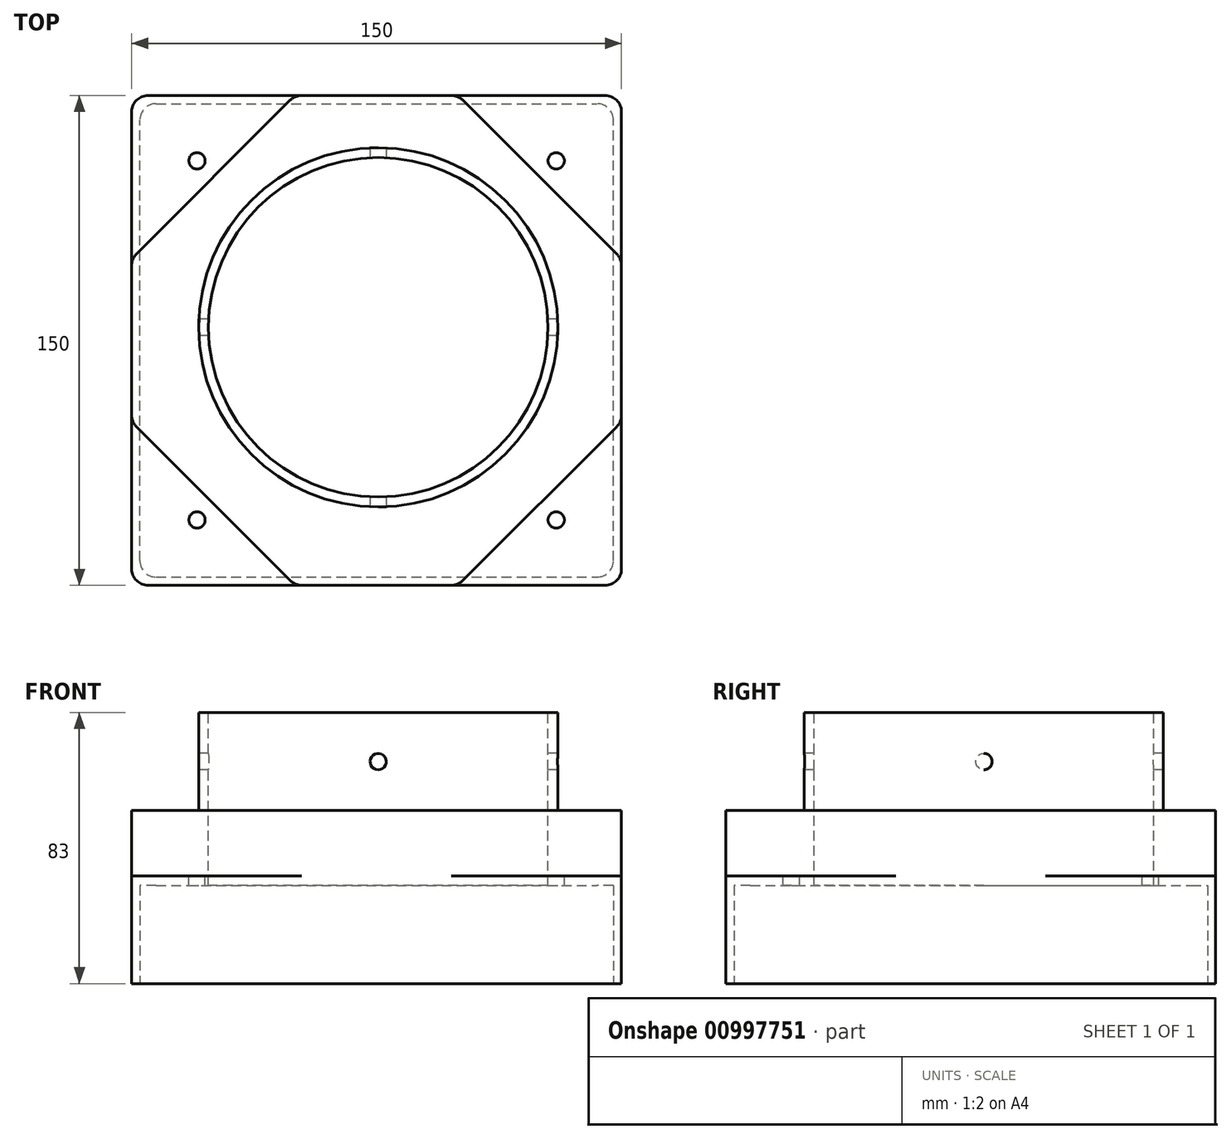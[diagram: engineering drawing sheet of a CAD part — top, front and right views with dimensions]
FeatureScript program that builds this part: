
annotation { "Feature Type Name" : "Feature", "Feature Type Description" : "" }
export const myFeature = defineFeature(function(context is Context, id is Id, definition is map)
    precondition{}
    {
        {
            var Q0;
            Q0=qCreatedBy(makeId("Top.planeOp"),FACE);
            var sketch = newSketch(context, id + "F0", { "sketchPlane" : qUnion([Q0])});
            skLineSegment(sketch, "E0.bottom", {"start": v(-75.5, 71) * mm, "end": v(74.5, 71) * mm});
            skLineSegment(sketch, "E0.top", {"start": v(-75.5, -79) * mm, "end": v(74.5, -79) * mm});
            skLineSegment(sketch, "E0.left", {"start": v(-75.5, 71) * mm, "end": v(-75.5, -79) * mm});
            skLineSegment(sketch, "E0.right", {"start": v(74.5, 71) * mm, "end": v(74.5, -79) * mm});
            skSolve(sketch);
        }
        {
            var Q0;
            Q0=makeQuery(id+"F0.imprint","IMPRINT",FACE,{"disambiguationData":[TD([[makeQuery(id+"F0.imprint","IMPRINT",EDGE,{"derivedFrom":sQuery(id+"F0.wireOp",EDGE,"E0.bottom")}),-1.0]])]});
            extrude(context, id + "F1", {"entities" : qUnion([Q0]), "depth" : 33 * mm, "offsetDistance" : 25 * mm});
        }
        {
            var Q0;
            Q0=makeQuery(id+"F1.opExtrude","CAP_FACE",FACE,{"disambiguationData":[OSD([sQuery(id+"F0.wireOp",EDGE,"E0.bottom"),sQuery(id+"F0.wireOp",EDGE,"E0.top"),sQuery(id+"F0.wireOp",EDGE,"E0.left"),sQuery(id+"F0.wireOp",EDGE,"E0.right")])],"isStart":false});
            var sketch = newSketch(context, id + "F2", { "sketchPlane" : qUnion([Q0])});
            skLineSegment(sketch, "E1.0", {"start": v(-8.5, 88) * mm, "end": v(7.5, 88) * mm});
            skLineSegment(sketch, "E1.1", {"start": v(7.5, 88) * mm, "end": v(91.5, 4) * mm});
            skLineSegment(sketch, "E1.2", {"start": v(91.5, 4) * mm, "end": v(91.5, -12) * mm});
            skLineSegment(sketch, "E1.3", {"start": v(91.5, -12) * mm, "end": v(7.5, -96) * mm});
            skLineSegment(sketch, "E1.4", {"start": v(7.5, -96) * mm, "end": v(-8.5, -96) * mm});
            skLineSegment(sketch, "E1.5", {"start": v(-8.5, -96) * mm, "end": v(-92.5, -12) * mm});
            skLineSegment(sketch, "E1.6", {"start": v(-92.5, -12) * mm, "end": v(-92.5, 4) * mm});
            skLineSegment(sketch, "E1.7", {"start": v(-92.5, 4) * mm, "end": v(-8.5, 88) * mm});
            skPoint(sketch, "E1.0.midPoint", {"position": v(-0.5, 88) * mm});
            skPoint(sketch, "E2", {"position": v(-25.5, 71) * mm});
            skPoint(sketch, "E3", {"position": v(24.5, -79) * mm});
            skPoint(sketch, "E4", {"position": v(-75.5, -29) * mm});
            skPoint(sketch, "E5", {"position": v(24.5, 71) * mm});
            skPoint(sketch, "E6", {"position": v(-75.5, 21) * mm});
            skPoint(sketch, "E7", {"position": v(74.5, 21) * mm});
            skPoint(sketch, "E8", {"position": v(74.5, -29) * mm});
            skPoint(sketch, "E9", {"position": v(-25.5, -79) * mm});
            skSolve(sketch);
        }
        {
            var Q0;
            {var subQ3=makeQuery(id+"F1.opExtrude","CAP_EDGE",EDGE,{"disambiguationData":[OSD([sQuery(id+"F0.wireOp",EDGE,"E0.bottom")])],"isStart":false});var subQ13=sQuery(id+"F2.wireOp",EDGE,"E1.1");var subQ14=makeQuery(id+"F2.imprint","INTERSECT",VERTEX,{"derivedFrom":[subQ3,subQ13]});Q0=makeQuery(id+"F2.imprint","IMPRINT",FACE,{"disambiguationData":[TD([[makeQuery(id+"F2.imprint","IMPRINT",EDGE,{"disambiguationData":[TD([[subQ14,-1.0]])],"derivedFrom":subQ13}),-1.0]])]});}
            extrude(context, id + "F3", {"entities" : qUnion([Q0]), "operationType" : NewBodyOperationType.ADD, "depth" : 20 * mm, "offsetDistance" : 25 * mm});
        }
        {
            var Q0;
            Q0=makeQuery(id+"F1.opExtrude","SWEPT_EDGE",EDGE,{"disambiguationData":[OSD([sQuery(id+"F0.wireOp",EDGE,"E0.bottom"),sQuery(id+"F0.wireOp",EDGE,"E0.left")])]});
            var Q1;
            Q1=makeQuery(id+"F1.opExtrude","SWEPT_EDGE",EDGE,{"disambiguationData":[OSD([sQuery(id+"F0.wireOp",EDGE,"E0.top"),sQuery(id+"F0.wireOp",EDGE,"E0.left")])]});
            var Q2;
            Q2=makeQuery(id+"F1.opExtrude","SWEPT_EDGE",EDGE,{"disambiguationData":[OSD([sQuery(id+"F0.wireOp",EDGE,"E0.bottom"),sQuery(id+"F0.wireOp",EDGE,"E0.right")])]});
            var Q3;
            Q3=makeQuery(id+"F1.opExtrude","SWEPT_EDGE",EDGE,{"disambiguationData":[OSD([sQuery(id+"F0.wireOp",EDGE,"E0.top"),sQuery(id+"F0.wireOp",EDGE,"E0.right")])]});
            fillet(context, id + "F4", {"entities" : qUnion([Q0, Q1, Q2, Q3]), "radius" : 5 * mm, "tangentPropagation" : true, "allowEdgeOverflow" : false});
        }
        {
            var Q0;
            Q0=makeQuery(id+"F3.opExtrude","CAP_FACE",FACE,{"disambiguationData":[OSD([sQuery(id+"F0.wireOp",EDGE,"E0.bottom"),sQuery(id+"F0.wireOp",EDGE,"E0.top"),sQuery(id+"F0.wireOp",EDGE,"E0.left"),sQuery(id+"F0.wireOp",EDGE,"E0.right"),sQuery(id+"F2.wireOp",EDGE,"E1.1"),sQuery(id+"F2.wireOp",EDGE,"E1.3"),sQuery(id+"F2.wireOp",EDGE,"E1.5"),sQuery(id+"F2.wireOp",EDGE,"E1.7")])],"isStart":false});
            var sketch = newSketch(context, id + "F5", { "sketchPlane" : qUnion([Q0])});
            skCircle(sketch, "E10", {"center": v(0, 0) * mm, "radius": 55 * mm});
            skSolve(sketch);
        }
        {
            var Q0;
            Q0 = qSketchRegion(id + "F5", true);
            extrude(context, id + "F6", {"entities" : qUnion([Q0]), "operationType" : NewBodyOperationType.ADD, "depth" : 30 * mm, "offsetDistance" : 25 * mm});
        }
        {
            var Q0;
            Q0=makeQuery(id+"F1.opExtrude","CAP_FACE",FACE,{"disambiguationData":[OSD([sQuery(id+"F0.wireOp",EDGE,"E0.bottom"),sQuery(id+"F0.wireOp",EDGE,"E0.top"),sQuery(id+"F0.wireOp",EDGE,"E0.left"),sQuery(id+"F0.wireOp",EDGE,"E0.right")])],"isStart":true});
            var sketch = newSketch(context, id + "F7", { "sketchPlane" : qUnion([Q0])});
            skLineSegment(sketch, "E11.bottom", {"start": v(-68, 76.5) * mm, "end": v(67, 76.5) * mm});
            skLineSegment(sketch, "E11.top", {"start": v(-68, -68.5) * mm, "end": v(67, -68.5) * mm});
            skLineSegment(sketch, "E11.left", {"start": v(-73, 71.5) * mm, "end": v(-73, -63.5) * mm});
            skLineSegment(sketch, "E11.right", {"start": v(72, 71.5) * mm, "end": v(72, -63.5) * mm});
            skPoint(sketch, "E12.visualSharp", {"position": v(-73, 76.5) * mm});
            skArc(sketch, "E12.filletArc", {"start": v(-68, 76.5) * mm, "mid": v(-71.54, 75.04) * mm, "end": v(-73, 71.5) * mm});
            skPoint(sketch, "E13.visualSharp", {"position": v(72, 76.5) * mm});
            skArc(sketch, "E13.filletArc", {"start": v(72, 71.5) * mm, "mid": v(70.54, 75.04) * mm, "end": v(67, 76.5) * mm});
            skPoint(sketch, "E14.visualSharp", {"position": v(72, -68.5) * mm});
            skArc(sketch, "E14.filletArc", {"start": v(67, -68.5) * mm, "mid": v(70.54, -67.03) * mm, "end": v(72, -63.5) * mm});
            skPoint(sketch, "E15.visualSharp", {"position": v(-73, -68.5) * mm});
            skArc(sketch, "E15.filletArc", {"start": v(-73, -63.5) * mm, "mid": v(-71.54, -67.03) * mm, "end": v(-68, -68.5) * mm});
            skSolve(sketch);
        }
        {
            var Q0;
            Q0=makeQuery(id+"F7.imprint","IMPRINT",FACE,{"disambiguationData":[TD([[makeQuery(id+"F7.imprint","IMPRINT",EDGE,{"derivedFrom":sQuery(id+"F7.wireOp",EDGE,"E11.bottom")}),-1.0]])]});
            extrude(context, id + "F8", {"entities" : qUnion([Q0]), "operationType" : NewBodyOperationType.REMOVE, "oppositeDirection" : true, "depth" : 30 * mm, "offsetDistance" : 25 * mm});
        }
        {
            var Q0;
            Q0=makeQuery(id+"F6.opExtrude","CAP_FACE",FACE,{"disambiguationData":[OSD([sQuery(id+"F5.wireOp",EDGE,"E10")])],"isStart":false});
            var sketch = newSketch(context, id + "F9", { "sketchPlane" : qUnion([Q0])});
            skCircle(sketch, "E16", {"center": v(0, 0) * mm, "radius": 52 * mm});
            skSolve(sketch);
        }
        {
            var Q0;
            Q0=makeQuery(id+"F9.imprint","IMPRINT",FACE,{"disambiguationData":[TD([[makeQuery(id+"F9.imprint","IMPRINT",EDGE,{"derivedFrom":sQuery(id+"F9.wireOp",EDGE,"E16")}),1.0]])]});
            extrude(context, id + "F10", {"entities" : qUnion([Q0]), "operationType" : NewBodyOperationType.REMOVE, "endBound" : BoundingType.THROUGH_ALL, "oppositeDirection" : true, "depth" : 25 * mm, "offsetDistance" : 25 * mm});
        }
        {
            var Q0;
            {var subQ0=sQuery(id+"F0.wireOp",EDGE,"E0.bottom");var subQ1=sQuery(id+"F0.wireOp",EDGE,"E0.left");Q0=makeQuery(id+"F3.boolean.opBoolean","SPLIT",FACE,{"disambiguationData":[TD([makeQuery(id+"F3.opExtrude","SWEPT_FACE",FACE,{"disambiguationData":[OSD([sQuery(id+"F2.wireOp",EDGE,"E1.7")])]})])],"derivedFrom":makeQuery(id+"F1.opExtrude","CAP_FACE",FACE,{"disambiguationData":[OSD([subQ0,sQuery(id+"F0.wireOp",EDGE,"E0.top"),subQ1,sQuery(id+"F0.wireOp",EDGE,"E0.right")])],"isStart":false})});}
            var sketch = newSketch(context, id + "F11", { "sketchPlane" : qUnion([Q0])});
            skPoint(sketch, "E17", {"position": v(-55.5, 51) * mm});
            skCircle(sketch, "E18", {"center": v(-55.5, 51) * mm, "radius": 2.5 * mm});
            skSolve(sketch);
        }
        {
            var Q0;
            Q0=makeQuery(id+"F11.imprint","IMPRINT",FACE,{"disambiguationData":[TD([[makeQuery(id+"F11.imprint","IMPRINT",EDGE,{"derivedFrom":sQuery(id+"F11.wireOp",EDGE,"E18")}),1.0]])]});
            extrude(context, id + "F12", {"entities" : qUnion([Q0]), "operationType" : NewBodyOperationType.REMOVE, "endBound" : BoundingType.THROUGH_ALL, "oppositeDirection" : true, "depth" : 25 * mm, "offsetDistance" : 25 * mm});
        }
        {
            var Q0;
            {var subQ0=sQuery(id+"F0.wireOp",EDGE,"E0.bottom");var subQ1=sQuery(id+"F0.wireOp",EDGE,"E0.right");Q0=makeQuery(id+"F3.boolean.opBoolean","SPLIT",FACE,{"disambiguationData":[TD([makeQuery(id+"F3.opExtrude","SWEPT_FACE",FACE,{"disambiguationData":[OSD([sQuery(id+"F2.wireOp",EDGE,"E1.1")])]})])],"derivedFrom":makeQuery(id+"F1.opExtrude","CAP_FACE",FACE,{"disambiguationData":[OSD([subQ0,sQuery(id+"F0.wireOp",EDGE,"E0.top"),sQuery(id+"F0.wireOp",EDGE,"E0.left"),subQ1])],"isStart":false})});}
            var sketch = newSketch(context, id + "F13", { "sketchPlane" : qUnion([Q0])});
            skPoint(sketch, "E19", {"position": v(54.5, 51) * mm});
            skCircle(sketch, "E20", {"center": v(54.5, 51) * mm, "radius": 2.5 * mm});
            skSolve(sketch);
        }
        {
            var Q0;
            Q0=makeQuery(id+"F13.imprint","IMPRINT",FACE,{"disambiguationData":[TD([[makeQuery(id+"F13.imprint","IMPRINT",EDGE,{"derivedFrom":sQuery(id+"F13.wireOp",EDGE,"E20")}),1.0]])]});
            extrude(context, id + "F14", {"entities" : qUnion([Q0]), "operationType" : NewBodyOperationType.REMOVE, "endBound" : BoundingType.THROUGH_ALL, "oppositeDirection" : true, "depth" : 25 * mm, "offsetDistance" : 25 * mm});
        }
        {
            var Q0;
            {var subQ0=sQuery(id+"F0.wireOp",EDGE,"E0.top");var subQ1=sQuery(id+"F0.wireOp",EDGE,"E0.left");Q0=makeQuery(id+"F3.boolean.opBoolean","SPLIT",FACE,{"disambiguationData":[TD([makeQuery(id+"F3.opExtrude","SWEPT_FACE",FACE,{"disambiguationData":[OSD([sQuery(id+"F2.wireOp",EDGE,"E1.5")])]})])],"derivedFrom":makeQuery(id+"F1.opExtrude","CAP_FACE",FACE,{"disambiguationData":[OSD([sQuery(id+"F0.wireOp",EDGE,"E0.bottom"),subQ0,subQ1,sQuery(id+"F0.wireOp",EDGE,"E0.right")])],"isStart":false})});}
            var sketch = newSketch(context, id + "F15", { "sketchPlane" : qUnion([Q0])});
            skPoint(sketch, "E21", {"position": v(-55.5, -59) * mm});
            skCircle(sketch, "E22", {"center": v(-55.5, -59) * mm, "radius": 2.5 * mm});
            skSolve(sketch);
        }
        {
            var Q0;
            Q0=makeQuery(id+"F15.imprint","IMPRINT",FACE,{"disambiguationData":[TD([[makeQuery(id+"F15.imprint","IMPRINT",EDGE,{"derivedFrom":sQuery(id+"F15.wireOp",EDGE,"E22")}),1.0]])]});
            extrude(context, id + "F16", {"entities" : qUnion([Q0]), "operationType" : NewBodyOperationType.REMOVE, "endBound" : BoundingType.THROUGH_ALL, "oppositeDirection" : true, "depth" : 25 * mm, "offsetDistance" : 25 * mm});
        }
        {
            var Q0;
            {var subQ0=sQuery(id+"F0.wireOp",EDGE,"E0.top");var subQ1=sQuery(id+"F0.wireOp",EDGE,"E0.right");Q0=makeQuery(id+"F3.boolean.opBoolean","SPLIT",FACE,{"disambiguationData":[TD([makeQuery(id+"F3.opExtrude","SWEPT_FACE",FACE,{"disambiguationData":[OSD([sQuery(id+"F2.wireOp",EDGE,"E1.3")])]})])],"derivedFrom":makeQuery(id+"F1.opExtrude","CAP_FACE",FACE,{"disambiguationData":[OSD([sQuery(id+"F0.wireOp",EDGE,"E0.bottom"),subQ0,sQuery(id+"F0.wireOp",EDGE,"E0.left"),subQ1])],"isStart":false})});}
            var sketch = newSketch(context, id + "F17", { "sketchPlane" : qUnion([Q0])});
            skPoint(sketch, "E23", {"position": v(54.5, -59) * mm});
            skCircle(sketch, "E24", {"center": v(54.5, -59) * mm, "radius": 2.5 * mm});
            skSolve(sketch);
        }
        {
            var Q0;
            Q0 = qSketchRegion(id + "F17", true);
            extrude(context, id + "F18", {"entities" : qUnion([Q0]), "operationType" : NewBodyOperationType.REMOVE, "endBound" : BoundingType.THROUGH_ALL, "oppositeDirection" : true, "depth" : 25 * mm, "offsetDistance" : 25 * mm});
        }
        {
            var Q0;
            Q0=makeQuery(id+"F3.opExtrude","SWEPT_EDGE",EDGE,{"disambiguationData":[OSD([sQuery(id+"F0.wireOp",EDGE,"E0.left"),sQuery(id+"F2.wireOp",EDGE,"E1.5")])]});
            var Q1;
            Q1=makeQuery(id+"F3.opExtrude","SWEPT_EDGE",EDGE,{"disambiguationData":[OSD([sQuery(id+"F0.wireOp",EDGE,"E0.left"),sQuery(id+"F2.wireOp",EDGE,"E1.7")])]});
            var Q2;
            Q2=makeQuery(id+"F3.opExtrude","SWEPT_EDGE",EDGE,{"disambiguationData":[OSD([sQuery(id+"F0.wireOp",EDGE,"E0.top"),sQuery(id+"F2.wireOp",EDGE,"E1.5")])]});
            var Q3;
            Q3=makeQuery(id+"F3.opExtrude","SWEPT_EDGE",EDGE,{"disambiguationData":[OSD([sQuery(id+"F0.wireOp",EDGE,"E0.top"),sQuery(id+"F2.wireOp",EDGE,"E1.3")])]});
            var Q4;
            Q4=makeQuery(id+"F3.opExtrude","SWEPT_EDGE",EDGE,{"disambiguationData":[OSD([sQuery(id+"F0.wireOp",EDGE,"E0.right"),sQuery(id+"F2.wireOp",EDGE,"E1.3")])]});
            var Q5;
            Q5=makeQuery(id+"F3.opExtrude","SWEPT_EDGE",EDGE,{"disambiguationData":[OSD([sQuery(id+"F0.wireOp",EDGE,"E0.right"),sQuery(id+"F2.wireOp",EDGE,"E1.1")])]});
            var Q6;
            Q6=makeQuery(id+"F3.opExtrude","SWEPT_EDGE",EDGE,{"disambiguationData":[OSD([sQuery(id+"F0.wireOp",EDGE,"E0.bottom"),sQuery(id+"F2.wireOp",EDGE,"E1.1")])]});
            var Q7;
            Q7=makeQuery(id+"F3.opExtrude","SWEPT_EDGE",EDGE,{"disambiguationData":[OSD([sQuery(id+"F0.wireOp",EDGE,"E0.bottom"),sQuery(id+"F2.wireOp",EDGE,"E1.7")])]});
            fillet(context, id + "F19", {"entities" : qUnion([Q0, Q1, Q2, Q3, Q4, Q5, Q6, Q7]), "radius" : 5 * mm, "tangentPropagation" : true, "allowEdgeOverflow" : false});
        }
        {
            var Q0;
            Q0=qCreatedBy(makeId("Right.planeOp"),FACE);
            var sketch = newSketch(context, id + "F20", { "sketchPlane" : qUnion([Q0])});
            skCircle(sketch, "E25", {"center": v(0, 68) * mm, "radius": 2.5 * mm});
            skSolve(sketch);
        }
        {
            var Q0;
            Q0=makeQuery(id+"F20.imprint","IMPRINT",FACE,{"disambiguationData":[TD([[makeQuery(id+"F20.imprint","IMPRINT",EDGE,{"derivedFrom":sQuery(id+"F20.wireOp",EDGE,"E25")}),1.0]])]});
            var Q1;
            Q1=sQuery(id+"F20.wireOp",EDGE,"E25");
            extrude(context, id + "F21", {"entities" : qUnion([Q0]), "operationType" : NewBodyOperationType.REMOVE, "surfaceEntities" : qUnion([Q1]), "endBound" : BoundingType.SYMMETRIC, "depth" : 150 * mm, "offsetDistance" : 25 * mm});
        }
        {
            var Q0;
            Q0=qCreatedBy(makeId("Front.planeOp"),FACE);
            var sketch = newSketch(context, id + "F22", { "sketchPlane" : qUnion([Q0])});
            skCircle(sketch, "E26", {"center": v(0, 68) * mm, "radius": 2.5 * mm});
            skSolve(sketch);
        }
        {
            var Q0;
            Q0=makeQuery(id+"F22.imprint","IMPRINT",FACE,{"disambiguationData":[TD([[makeQuery(id+"F22.imprint","IMPRINT",EDGE,{"derivedFrom":sQuery(id+"F22.wireOp",EDGE,"E26")}),1.0]])]});
            extrude(context, id + "F23", {"entities" : qUnion([Q0]), "operationType" : NewBodyOperationType.REMOVE, "endBound" : BoundingType.SYMMETRIC, "oppositeDirection" : true, "depth" : 150 * mm, "offsetDistance" : 25 * mm});
        }
    });
